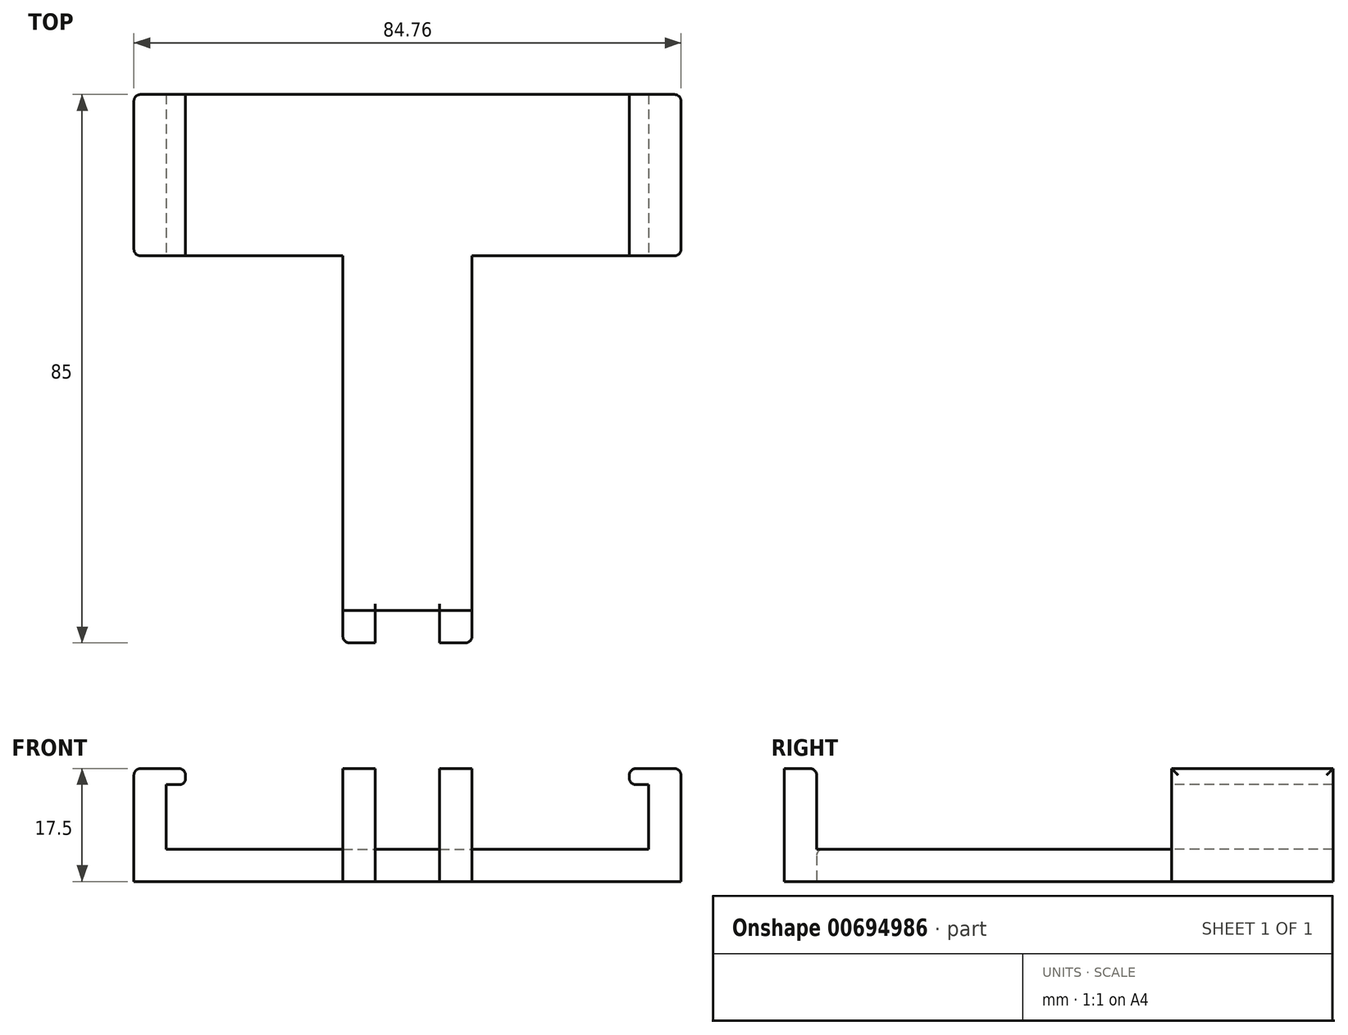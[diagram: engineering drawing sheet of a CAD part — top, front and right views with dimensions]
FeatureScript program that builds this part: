
annotation { "Feature Type Name" : "Feature", "Feature Type Description" : "" }
export const myFeature = defineFeature(function(context is Context, id is Id, definition is map)
    precondition{}
    {
        {
            var Q0;
            Q0=qCreatedBy(makeId("Top.planeOp"),FACE);
            var sketch = newSketch(context, id + "F0", { "sketchPlane" : qUnion([Q0])});
            skLineSegment(sketch, "E0.bottom", {"start": v(-37.38, 12.5) * mm, "end": v(37.38, 12.5) * mm});
            skLineSegment(sketch, "E0.top", {"start": v(-37.38, -12.5) * mm, "end": v(37.38, -12.5) * mm});
            skLineSegment(sketch, "E0.left", {"start": v(-37.38, 12.5) * mm, "end": v(-37.38, -12.5) * mm});
            skLineSegment(sketch, "E0.right", {"start": v(37.38, 12.5) * mm, "end": v(37.38, -12.5) * mm});
            skPoint(sketch, "E1", {"position": v(0, 12.5) * mm});
            skPoint(sketch, "E2", {"position": v(-37.38, 0) * mm});
            skLineSegment(sketch, "E3.bottom", {"start": v(-10, 12.5) * mm, "end": v(10, 12.5) * mm});
            skLineSegment(sketch, "E3.top", {"start": v(-10, -67.5) * mm, "end": v(10, -67.5) * mm});
            skLineSegment(sketch, "E3.left", {"start": v(-10, 12.5) * mm, "end": v(-10, -67.5) * mm});
            skLineSegment(sketch, "E3.right", {"start": v(10, 12.5) * mm, "end": v(10, -67.5) * mm});
            skSolve(sketch);
        }
        {
            var Q0;
            Q0=qSketchRegion(id+"F0",true);
            extrude(context, id + "F1", {"entities" : qUnion([Q0]), "depth" : 5 * mm, "offsetDistance" : 25 * mm});
        }
        {
            var Q0;
            Q0=qCreatedBy(makeId("Top.planeOp"),FACE);
            var sketch = newSketch(context, id + "F2", { "sketchPlane" : qUnion([Q0])});
            skLineSegment(sketch, "E4.bottom", {"start": v(-42.37, 12.5) * mm, "end": v(-37.38, 12.5) * mm});
            skLineSegment(sketch, "E4.top", {"start": v(-42.37, -12.5) * mm, "end": v(-37.38, -12.5) * mm});
            skLineSegment(sketch, "E4.left", {"start": v(-42.37, 12.5) * mm, "end": v(-42.37, -12.5) * mm});
            skLineSegment(sketch, "E4.right", {"start": v(-37.38, 12.5) * mm, "end": v(-37.38, -12.5) * mm});
            skLineSegment(sketch, "E5.MirrorCS", {"start": v(42.37, 12.5) * mm, "end": v(37.38, 12.5) * mm});
            skLineSegment(sketch, "E6.MirrorCS", {"start": v(42.37, 12.5) * mm, "end": v(42.37, -12.5) * mm});
            skLineSegment(sketch, "E7.MirrorCS", {"start": v(42.37, -12.5) * mm, "end": v(37.38, -12.5) * mm});
            skLineSegment(sketch, "E8.MirrorCS", {"start": v(37.38, 12.5) * mm, "end": v(37.38, -12.5) * mm});
            skLineSegment(sketch, "E9.bottom", {"start": v(-10, -67.5) * mm, "end": v(-5, -67.5) * mm});
            skLineSegment(sketch, "E9.top", {"start": v(-10, -72.5) * mm, "end": v(-5, -72.5) * mm});
            skLineSegment(sketch, "E9.left", {"start": v(-10, -67.5) * mm, "end": v(-10, -72.5) * mm});
            skLineSegment(sketch, "E9.right", {"start": v(-5, -67.5) * mm, "end": v(-5, -72.5) * mm});
            skLineSegment(sketch, "E10.MirrorCS", {"start": v(5, -67.5) * mm, "end": v(5, -72.5) * mm});
            skLineSegment(sketch, "E11.MirrorCS", {"start": v(10, -67.5) * mm, "end": v(10, -72.5) * mm});
            skLineSegment(sketch, "E12.MirrorCS", {"start": v(10, -67.5) * mm, "end": v(5, -67.5) * mm});
            skLineSegment(sketch, "E13.MirrorCS", {"start": v(10, -72.5) * mm, "end": v(5, -72.5) * mm});
            skSolve(sketch);
        }
        {
            var Q0;
            Q0=qSketchRegion(id+"F2",true);
            extrude(context, id + "F3", {"entities" : qUnion([Q0]), "operationType" : NewBodyOperationType.ADD, "depth" : 17.5 * mm, "offsetDistance" : 25 * mm});
        }
        {
            var Q0;
            Q0=makeQuery(id+"F3.opExtrude","SWEPT_FACE",FACE,{"disambiguationData":[OSD([sQuery(id+"F2.wireOp",EDGE,"E4.right")])]});
            var sketch = newSketch(context, id + "F4", { "sketchPlane" : qUnion([Q0])});
            skLineSegment(sketch, "E14", {"start": v(-12.5, 15) * mm, "end": v(12.5, 15) * mm});
            skLineSegment(sketch, "E15", {"start": v(-12.5, 15) * mm, "end": v(-12.5, 17.5) * mm});
            skLineSegment(sketch, "E16", {"start": v(-12.5, 17.5) * mm, "end": v(12.5, 17.5) * mm});
            skLineSegment(sketch, "E17", {"start": v(12.5, 17.5) * mm, "end": v(12.5, 15) * mm});
            skSolve(sketch);
        }
        {
            var Q0;
            Q0=qSketchRegion(id+"F4",true);
            extrude(context, id + "F5", {"entities" : qUnion([Q0]), "operationType" : NewBodyOperationType.ADD, "depth" : 3 * mm, "offsetDistance" : 25 * mm});
        }
        {
            var Q0;
            Q0=makeQuery(id+"F3.opExtrude","SWEPT_FACE",FACE,{"disambiguationData":[OSD([sQuery(id+"F2.wireOp",EDGE,"E8.MirrorCS")])]});
            var sketch = newSketch(context, id + "F6", { "sketchPlane" : qUnion([Q0])});
            skLineSegment(sketch, "E18", {"start": v(-12.5, 15) * mm, "end": v(12.5, 15) * mm});
            skLineSegment(sketch, "E19", {"start": v(-12.5, 15) * mm, "end": v(-12.5, 17.5) * mm});
            skLineSegment(sketch, "E20", {"start": v(-12.5, 17.5) * mm, "end": v(12.5, 17.5) * mm});
            skLineSegment(sketch, "E21", {"start": v(12.5, 17.5) * mm, "end": v(12.5, 15) * mm});
            skSolve(sketch);
        }
        {
            var Q0;
            Q0=qSketchRegion(id+"F6",true);
            extrude(context, id + "F7", {"entities" : qUnion([Q0]), "operationType" : NewBodyOperationType.ADD, "depth" : 3 * mm, "offsetDistance" : 25 * mm});
        }
        {
            var Q0;
            Q0=makeQuery(id+"F1.opExtrude","CAP_EDGE",EDGE,{"disambiguationData":[OSD([sQuery(id+"F0.wireOp",EDGE,"E0.left")])],"isStart":false});
            var Q1;
            Q1=makeQuery(id+"F1.opExtrude","CAP_EDGE",EDGE,{"disambiguationData":[OSD([sQuery(id+"F0.wireOp",EDGE,"E0.right")])],"isStart":false});
            var Q2;
            Q2=makeQuery(id+"F3.opExtrude","CAP_EDGE",EDGE,{"disambiguationData":[OSD([sQuery(id+"F2.wireOp",EDGE,"E12.MirrorCS")])],"isStart":false});
            var Q3;
            Q3=makeQuery(id+"F3.opExtrude","CAP_EDGE",EDGE,{"disambiguationData":[OSD([sQuery(id+"F2.wireOp",EDGE,"E9.bottom")])],"isStart":false});
            var Q4;
            {var subQ0=sQuery(id+"F0.wireOp",EDGE,"E3.top");Q4=makeQuery(id+"F3.boolean.opBoolean","SPLIT",EDGE,{"disambiguationData":[topologyDisambiguationEdgeConnected([makeQuery(id+"F3.opExtrude","SWEPT_FACE",FACE,{"disambiguationData":[OSD([sQuery(id+"F2.wireOp",EDGE,"E12.MirrorCS")])]})])],"derivedFrom":makeQuery(id+"F1.opExtrude","CAP_EDGE",EDGE,{"disambiguationData":[OSD([subQ0])],"isStart":false})});}
            var Q5;
            {var subQ0=sQuery(id+"F0.wireOp",EDGE,"E3.top");Q5=makeQuery(id+"F3.boolean.opBoolean","SPLIT",EDGE,{"disambiguationData":[topologyDisambiguationEdgeConnected([makeQuery(id+"F3.opExtrude","SWEPT_FACE",FACE,{"disambiguationData":[OSD([sQuery(id+"F2.wireOp",EDGE,"E9.bottom")])]})])],"derivedFrom":makeQuery(id+"F1.opExtrude","CAP_EDGE",EDGE,{"disambiguationData":[OSD([subQ0])],"isStart":false})});}
            var Q6;
            Q6=makeQuery(id+"F3.opExtrude","SWEPT_EDGE",EDGE,{"disambiguationData":[OSD([sQuery(id+"F2.wireOp",EDGE,"E4.top"),sQuery(id+"F2.wireOp",EDGE,"E4.left")])]});
            var Q7;
            Q7=makeQuery(id+"F3.opExtrude","SWEPT_EDGE",EDGE,{"disambiguationData":[OSD([sQuery(id+"F2.wireOp",EDGE,"E4.bottom"),sQuery(id+"F2.wireOp",EDGE,"E4.left")])]});
            var Q8;
            Q8=makeQuery(id+"F3.opExtrude","CAP_EDGE",EDGE,{"disambiguationData":[OSD([sQuery(id+"F2.wireOp",EDGE,"E4.left")])],"isStart":false});
            var Q9;
            Q9=makeQuery(id+"F3.opExtrude","CAP_EDGE",EDGE,{"disambiguationData":[OSD([sQuery(id+"F2.wireOp",EDGE,"E6.MirrorCS")])],"isStart":false});
            var Q10;
            Q10=makeQuery(id+"F3.opExtrude","SWEPT_EDGE",EDGE,{"disambiguationData":[OSD([sQuery(id+"F2.wireOp",EDGE,"E6.MirrorCS"),sQuery(id+"F2.wireOp",EDGE,"E7.MirrorCS")])]});
            var Q11;
            Q11=makeQuery(id+"F3.opExtrude","SWEPT_EDGE",EDGE,{"disambiguationData":[OSD([sQuery(id+"F2.wireOp",EDGE,"E5.MirrorCS"),sQuery(id+"F2.wireOp",EDGE,"E6.MirrorCS")])]});
            var Q12;
            Q12=makeQuery(id+"F3.opExtrude","SWEPT_EDGE",EDGE,{"disambiguationData":[OSD([sQuery(id+"F2.wireOp",EDGE,"E9.top"),sQuery(id+"F2.wireOp",EDGE,"E9.left")])]});
            var Q13;
            Q13=makeQuery(id+"F3.opExtrude","SWEPT_EDGE",EDGE,{"disambiguationData":[OSD([sQuery(id+"F2.wireOp",EDGE,"E11.MirrorCS"),sQuery(id+"F2.wireOp",EDGE,"E13.MirrorCS")])]});
            var Q14;
            Q14=makeQuery(id+"F5.opExtrude","CAP_EDGE",EDGE,{"disambiguationData":[OSD([sQuery(id+"F4.wireOp",EDGE,"E16")])],"isStart":false});
            var Q15;
            Q15=makeQuery(id+"F5.opExtrude","CAP_EDGE",EDGE,{"disambiguationData":[OSD([sQuery(id+"F4.wireOp",EDGE,"E14")])],"isStart":false});
            var Q16;
            Q16=makeQuery(id+"F7.opExtrude","CAP_EDGE",EDGE,{"disambiguationData":[OSD([sQuery(id+"F6.wireOp",EDGE,"E20")])],"isStart":false});
            var Q17;
            Q17=makeQuery(id+"F7.opExtrude","CAP_EDGE",EDGE,{"disambiguationData":[OSD([sQuery(id+"F6.wireOp",EDGE,"E18")])],"isStart":false});
            var Q18;
            Q18=makeQuery(id+"F7.opExtrude","CAP_EDGE",EDGE,{"disambiguationData":[OSD([sQuery(id+"F6.wireOp",EDGE,"E18")])],"isStart":true});
            var Q19;
            Q19=makeQuery(id+"F5.opExtrude","CAP_EDGE",EDGE,{"disambiguationData":[OSD([sQuery(id+"F4.wireOp",EDGE,"E14")])],"isStart":true});
            fillet(context, id + "F8", {"entities" : qUnion([Q0, Q1, Q2, Q3, Q4, Q5, Q6, Q7, Q8, Q9, Q10, Q11, Q12, Q13, Q14, Q15, Q16, Q17, Q18, Q19]), "radius" : 1 * mm, "tangentPropagation" : true, "allowEdgeOverflow" : false});
        }
    });
